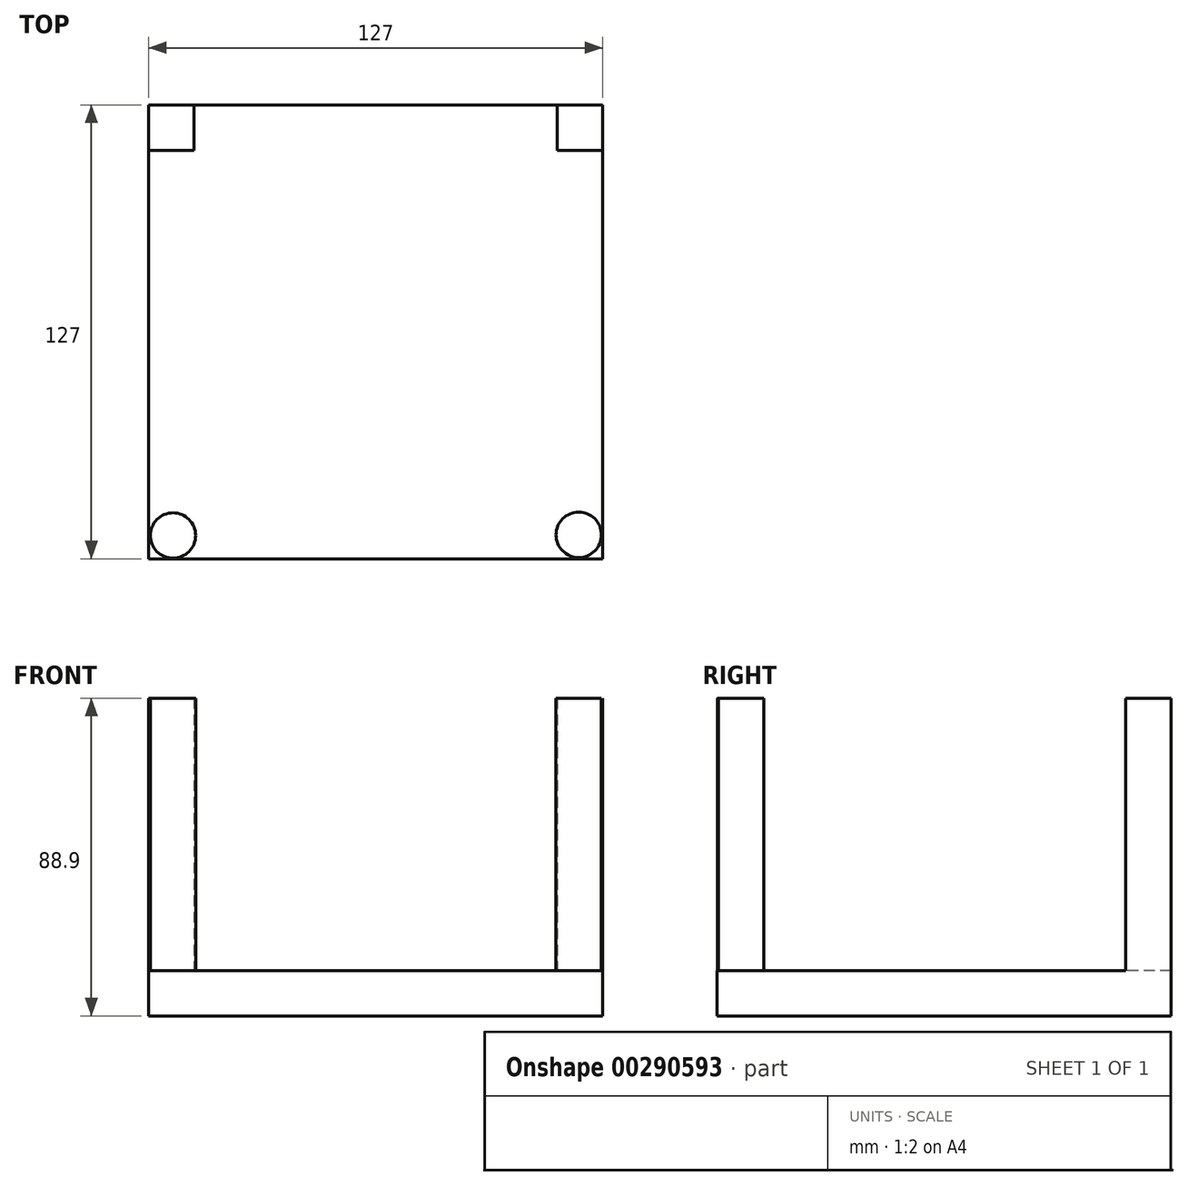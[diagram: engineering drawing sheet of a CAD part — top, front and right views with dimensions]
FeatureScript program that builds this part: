
annotation { "Feature Type Name" : "Feature", "Feature Type Description" : "" }
export const myFeature = defineFeature(function(context is Context, id is Id, definition is map)
    precondition{}
    {
        {
            var Q0;
            Q0=qCreatedBy(makeId("Top.planeOp"),FACE);
            var sketch = newSketch(context, id + "F0", { "sketchPlane" : qUnion([Q0])});
            skLineSegment(sketch, "E0.bottom", {"start": v(0, 0) * mm, "end": v(-127, 0) * mm});
            skLineSegment(sketch, "E0.top", {"start": v(0, -127) * mm, "end": v(-127, -127) * mm});
            skLineSegment(sketch, "E0.left", {"start": v(0, 0) * mm, "end": v(0, -127) * mm});
            skLineSegment(sketch, "E0.right", {"start": v(-127, 0) * mm, "end": v(-127, -127) * mm});
            skSolve(sketch);
        }
        {
            var Q0;
            Q0=makeQuery(id+"F0.imprint","IMPRINT",FACE,{"disambiguationData":[TD([[makeQuery(id+"F0.imprint","IMPRINT",EDGE,{"derivedFrom":sQuery(id+"F0.wireOp",EDGE,"E0.bottom")}),1.0]])]});
            extrude(context, id + "F1", {"entities" : qUnion([Q0]), "depth" : 12.7 * mm});
        }
        {
            var Q0;
            Q0=makeQuery(id+"F1.opExtrude","CAP_FACE",FACE,{"disambiguationData":[OSD([sQuery(id+"F0.wireOp",EDGE,"E0.bottom"),sQuery(id+"F0.wireOp",EDGE,"E0.top"),sQuery(id+"F0.wireOp",EDGE,"E0.left"),sQuery(id+"F0.wireOp",EDGE,"E0.right")])],"isStart":false});
            var sketch = newSketch(context, id + "F2", { "sketchPlane" : qUnion([Q0])});
            skLineSegment(sketch, "E1.bottom", {"start": v(-127, 0) * mm, "end": v(-114.3, 0) * mm});
            skLineSegment(sketch, "E1.top", {"start": v(-127, -12.7) * mm, "end": v(-114.3, -12.7) * mm});
            skLineSegment(sketch, "E1.left", {"start": v(-127, 0) * mm, "end": v(-127, -12.7) * mm});
            skLineSegment(sketch, "E1.right", {"start": v(-114.3, 0) * mm, "end": v(-114.3, -12.7) * mm});
            skLineSegment(sketch, "E2.bottom", {"start": v(0, 0) * mm, "end": v(-12.7, 0) * mm});
            skLineSegment(sketch, "E2.top", {"start": v(0, -12.7) * mm, "end": v(-12.7, -12.7) * mm});
            skLineSegment(sketch, "E2.left", {"start": v(0, 0) * mm, "end": v(0, -12.7) * mm});
            skLineSegment(sketch, "E2.right", {"start": v(-12.7, 0) * mm, "end": v(-12.7, -12.7) * mm});
            skCircle(sketch, "E3", {"center": v(-120.19, -120.5) * mm, "radius": 6.35 * mm});
            skCircle(sketch, "E4", {"center": v(-6.67, -120.31) * mm, "radius": 6.35 * mm});
            skSolve(sketch);
        }
        {
            var Q0;
            Q0=makeQuery(id+"F2.imprint","IMPRINT",FACE,{"disambiguationData":[TD([[makeQuery(id+"F2.imprint","IMPRINT",EDGE,{"derivedFrom":sQuery(id+"F2.wireOp",EDGE,"E1.bottom")}),1.0]])]});
            var Q1;
            Q1=makeQuery(id+"F2.imprint","IMPRINT",FACE,{"disambiguationData":[TD([[makeQuery(id+"F2.imprint","IMPRINT",EDGE,{"derivedFrom":sQuery(id+"F2.wireOp",EDGE,"E2.bottom")}),1.0]])]});
            var Q2;
            {var subQ0=sQuery(id+"F2.wireOp",EDGE,"E4");var subQ1=makeQuery(id+"F1.opExtrude","CAP_EDGE",EDGE,{"disambiguationData":[OSD([sQuery(id+"F0.wireOp",EDGE,"E0.top")])],"isStart":false});var subQ2=makeQuery(id+"F2.imprint","INTERSECT",VERTEX,{"derivedFrom":[subQ1,subQ0]});Q2=makeQuery(id+"F2.imprint","IMPRINT",FACE,{"disambiguationData":[TD([[makeQuery(id+"F2.imprint","IMPRINT",EDGE,{"disambiguationData":[TD([[subQ2,1.0]])],"derivedFrom":subQ0}),1.0]])]});}
            var Q3;
            {var subQ0=sQuery(id+"F2.wireOp",EDGE,"E4");var subQ1=makeQuery(id+"F1.opExtrude","CAP_EDGE",EDGE,{"disambiguationData":[OSD([sQuery(id+"F0.wireOp",EDGE,"E0.top")])],"isStart":false});var subQ2=makeQuery(id+"F2.imprint","INTERSECT",VERTEX,{"derivedFrom":[subQ1,subQ0]});Q3=makeQuery(id+"F2.imprint","IMPRINT",FACE,{"disambiguationData":[TD([[makeQuery(id+"F2.imprint","IMPRINT",EDGE,{"disambiguationData":[TD([[subQ2,-1.0]])],"derivedFrom":subQ0}),1.0]])]});}
            var Q4;
            {var subQ0=sQuery(id+"F2.wireOp",EDGE,"E3");var subQ1=makeQuery(id+"F1.opExtrude","CAP_EDGE",EDGE,{"disambiguationData":[OSD([sQuery(id+"F0.wireOp",EDGE,"E0.top")])],"isStart":false});var subQ2=makeQuery(id+"F2.imprint","INTERSECT",VERTEX,{"derivedFrom":[subQ1,subQ0]});Q4=makeQuery(id+"F2.imprint","IMPRINT",FACE,{"disambiguationData":[TD([[makeQuery(id+"F2.imprint","IMPRINT",EDGE,{"disambiguationData":[TD([[subQ2,-1.0]])],"derivedFrom":subQ0}),1.0]])]});}
            var Q5;
            {var subQ0=sQuery(id+"F2.wireOp",EDGE,"E3");var subQ1=makeQuery(id+"F1.opExtrude","CAP_EDGE",EDGE,{"disambiguationData":[OSD([sQuery(id+"F0.wireOp",EDGE,"E0.top")])],"isStart":false});var subQ2=makeQuery(id+"F2.imprint","INTERSECT",VERTEX,{"derivedFrom":[subQ1,subQ0]});Q5=makeQuery(id+"F2.imprint","IMPRINT",FACE,{"disambiguationData":[TD([[makeQuery(id+"F2.imprint","IMPRINT",EDGE,{"disambiguationData":[TD([[subQ2,1.0]])],"derivedFrom":subQ0}),1.0]])]});}
            extrude(context, id + "F3", {"entities" : qUnion([Q0, Q1, Q2, Q3, Q4, Q5]), "operationType" : NewBodyOperationType.ADD, "depth" : 76.2 * mm});
        }
    });
